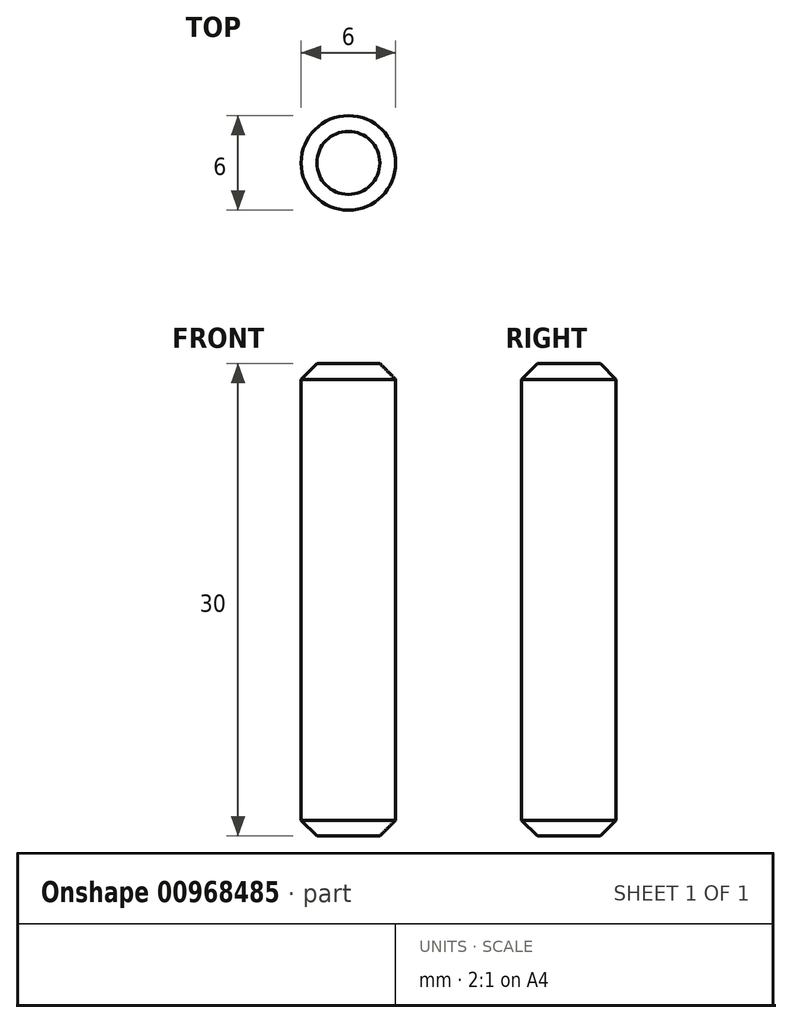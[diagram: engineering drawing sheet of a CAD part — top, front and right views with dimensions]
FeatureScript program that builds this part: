
annotation { "Feature Type Name" : "Feature", "Feature Type Description" : "" }
export const myFeature = defineFeature(function(context is Context, id is Id, definition is map)
    precondition{}
    {
        {
            var Q0;
            Q0=qCreatedBy(makeId("Top.planeOp"),FACE);
            var sketch = newSketch(context, id + "F0", { "sketchPlane" : qUnion([Q0])});
            skCircle(sketch, "E0.1.0", {"center": v(0, 0) * mm, "radius": 3 * mm});
            skPoint(sketch, "E0.center", {"position": v(0, 0) * mm});
            skSolve(sketch);
        }
        {
            var Q0;
            Q0=qSketchRegion(id+"F0",true);
            extrude(context, id + "F1", {"entities" : qUnion([Q0]), "depth" : 30 * mm, "offsetDistance" : 25 * mm});
        }
        {
            var Q0;
            Q0=makeQuery(id+"F1.opExtrude","CAP_EDGE",EDGE,{"disambiguationData":[OSD([sQuery(id+"F0.wireOp",EDGE,"E0.1.0")])],"isStart":false});
            var Q1;
            Q1=makeQuery(id+"F1.opExtrude","CAP_EDGE",EDGE,{"disambiguationData":[OSD([sQuery(id+"F0.wireOp",EDGE,"E0.1.0")])],"isStart":true});
            chamfer(context, id + "F2", {"entities" : qUnion([Q0, Q1]), "width" : 1 * mm, "tangentPropagation" : true});
        }
    });
